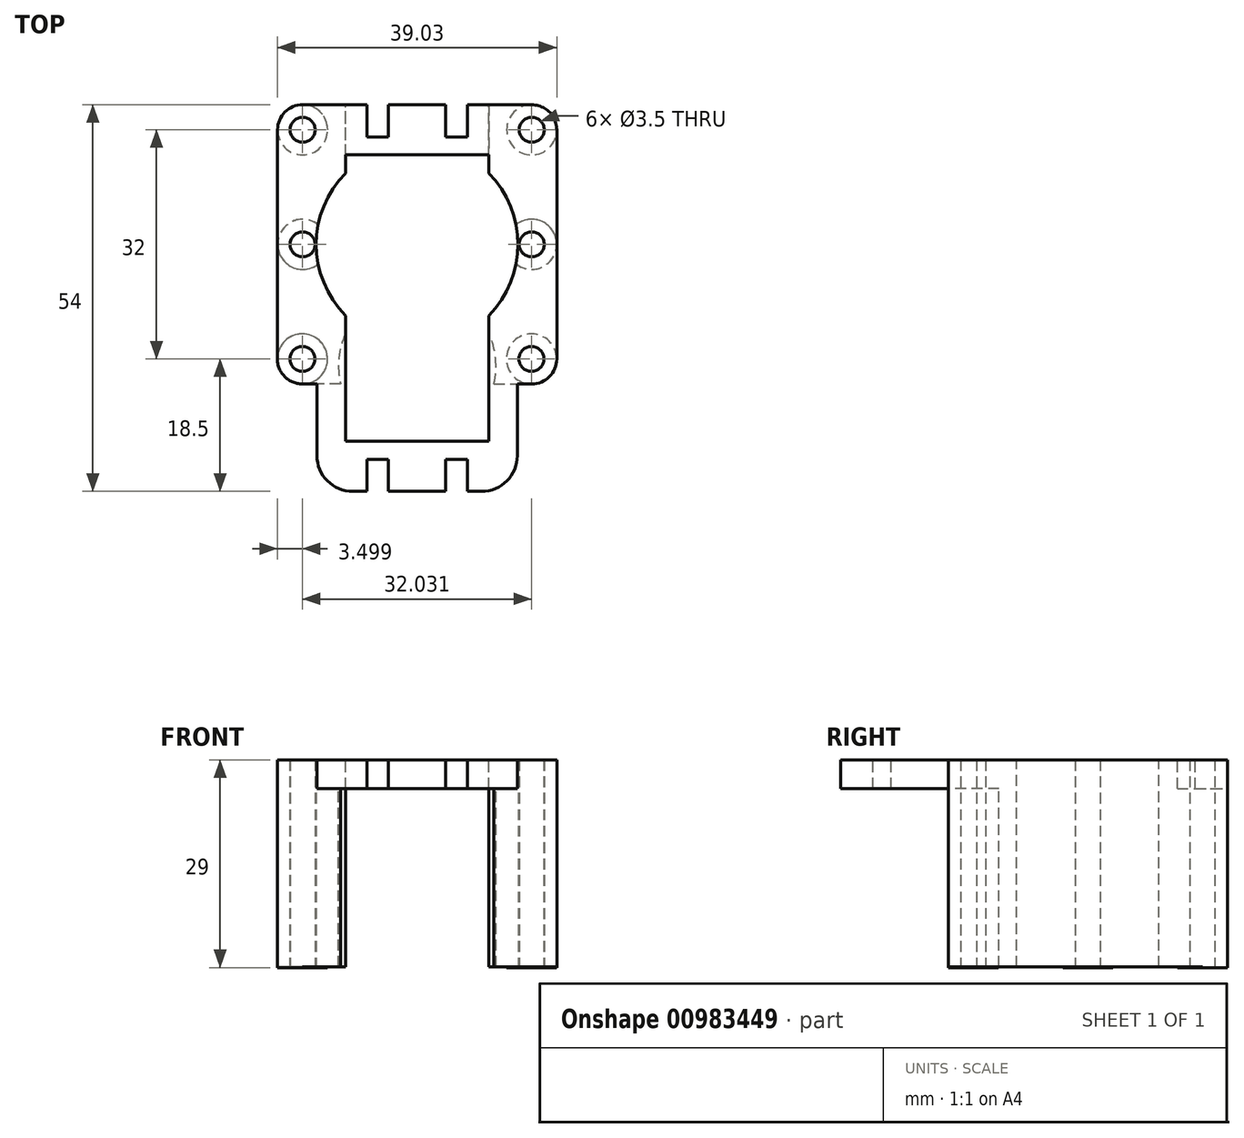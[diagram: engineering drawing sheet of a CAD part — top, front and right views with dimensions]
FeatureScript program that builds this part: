
annotation { "Feature Type Name" : "Feature", "Feature Type Description" : "" }
export const myFeature = defineFeature(function(context is Context, id is Id, definition is map)
    precondition{}
    {
        {
            var Q0;
            Q0=qCreatedBy(makeId("Top.planeOp"),FACE);
            var sketch = newSketch(context, id + "F0", { "sketchPlane" : qUnion([Q0])});
            skCircle(sketch, "E0", {"center": v(-16, 16) * mm, "radius": 3.5 * mm});
            skCircle(sketch, "E1", {"center": v(16, 16) * mm, "radius": 3.5 * mm});
            skCircle(sketch, "E2", {"center": v(15.97, -16) * mm, "radius": 3.5 * mm});
            skCircle(sketch, "E3", {"center": v(-16.03, -16) * mm, "radius": 3.5 * mm});
            skCircle(sketch, "E4", {"center": v(-16, 16) * mm, "radius": 1.75 * mm});
            skCircle(sketch, "E5", {"center": v(16, 16) * mm, "radius": 1.75 * mm});
            skCircle(sketch, "E6", {"center": v(-16.03, -16) * mm, "radius": 1.75 * mm});
            skCircle(sketch, "E7", {"center": v(15.97, -16) * mm, "radius": 1.75 * mm});
            skCircle(sketch, "E8", {"center": v(16, 0) * mm, "radius": 3.5 * mm});
            skCircle(sketch, "E9", {"center": v(16, 0) * mm, "radius": 1.75 * mm});
            skCircle(sketch, "E10", {"center": v(-16, 0) * mm, "radius": 1.75 * mm});
            skCircle(sketch, "E11", {"center": v(-16, 0) * mm, "radius": 3.5 * mm});
            skCircle(sketch, "E12", {"center": v(0, 0) * mm, "radius": 14.1 * mm});
            skSolve(sketch);
        }
        {
            var Q0;
            Q0=makeQuery(id+"F0.imprint","IMPRINT",FACE,{"disambiguationData":[TD([[makeQuery(id+"F0.imprint","IMPRINT",EDGE,{"derivedFrom":sQuery(id+"F0.wireOp",EDGE,"E0")}),1.0]])]});
            var Q1;
            Q1=makeQuery(id+"F0.imprint","IMPRINT",FACE,{"disambiguationData":[TD([[makeQuery(id+"F0.imprint","IMPRINT",EDGE,{"derivedFrom":sQuery(id+"F0.wireOp",EDGE,"E1")}),1.0]])]});
            var Q2;
            Q2=makeQuery(id+"F0.imprint","IMPRINT",FACE,{"disambiguationData":[TD([[makeQuery(id+"F0.imprint","IMPRINT",EDGE,{"derivedFrom":sQuery(id+"F0.wireOp",EDGE,"E2")}),1.0]])]});
            var Q3;
            Q3=makeQuery(id+"F0.imprint","IMPRINT",FACE,{"disambiguationData":[TD([[makeQuery(id+"F0.imprint","IMPRINT",EDGE,{"derivedFrom":sQuery(id+"F0.wireOp",EDGE,"E3")}),1.0]])]});
            var Q4;
            {var subQ0=sQuery(id+"F0.wireOp",EDGE,"aDhAWXYM-tOJJ-d5Va-h822-jFobYjWTLzZv");var subQ1=sQuery(id+"F0.wireOp",EDGE,"E8");var subQ2=makeQuery(id+"F0.imprint","INTERSECT",VERTEX,{"disambiguationData":[OD(0.0)],"derivedFrom":[subQ1,subQ0]});Q4=makeQuery(id+"F0.imprint","IMPRINT",FACE,{"disambiguationData":[TD([[makeQuery(id+"F0.imprint","IMPRINT",EDGE,{"disambiguationData":[TD([[subQ2,1.0]])],"derivedFrom":subQ1}),1.0]])]});}
            var Q5;
            {var subQ0=sQuery(id+"F0.wireOp",EDGE,"aDhAWXYM-tOJJ-d5Va-h822-jFobYjWTLzZv");var subQ1=sQuery(id+"F0.wireOp",EDGE,"E10");var subQ2=makeQuery(id+"F0.imprint","INTERSECT",VERTEX,{"disambiguationData":[OD(0.0)],"derivedFrom":[subQ1,subQ0]});Q5=makeQuery(id+"F0.imprint","IMPRINT",FACE,{"disambiguationData":[TD([[makeQuery(id+"F0.imprint","IMPRINT",EDGE,{"disambiguationData":[TD([[subQ2,-1.0]])],"derivedFrom":subQ1}),-1.0]])]});}
            extrude(context, id + "F1", {"entities" : qUnion([Q0, Q1, Q2, Q3, Q4, Q5]), "depth" : 29 * mm, "offsetDistance" : 25 * mm});
        }
        {
            var Q0;
            Q0=makeQuery(id+"F1.opExtrude","CAP_FACE",FACE,{"disambiguationData":[OSD([sQuery(id+"F0.wireOp",EDGE,"E0"),sQuery(id+"F0.wireOp",EDGE,"E4")])],"isStart":false});
            var sketch = newSketch(context, id + "F2", { "sketchPlane" : qUnion([Q0])});
            skLineSegment(sketch, "E13.bottom", {"start": v(10, -19.5) * mm, "end": v(-10, -19.5) * mm});
            skLineSegment(sketch, "E13.top", {"start": v(10, 19.5) * mm, "end": v(-10, 19.5) * mm});
            skLineSegment(sketch, "E13.left", {"start": v(10, -19.5) * mm, "end": v(10, 19.5) * mm});
            skLineSegment(sketch, "E13.right", {"start": v(-10, -19.5) * mm, "end": v(-10, 19.5) * mm});
            skPoint(sketch, "E13.middle", {"position": v(0, 0) * mm});
            skLineSegment(sketch, "E14.bottom", {"start": v(-10, 19.5) * mm, "end": v(-16, 19.5) * mm});
            skLineSegment(sketch, "E14.top", {"start": v(-10, -19.5) * mm, "end": v(-16, -19.5) * mm});
            skLineSegment(sketch, "E14.left", {"start": v(-10, 19.5) * mm, "end": v(-10, -19.5) * mm});
            skLineSegment(sketch, "E14.right", {"start": v(-19.5, 16) * mm, "end": v(-19.5, -16) * mm});
            skLineSegment(sketch, "E15.bottom", {"start": v(10, 19.5) * mm, "end": v(16, 19.5) * mm});
            skLineSegment(sketch, "E15.top", {"start": v(10, -19.5) * mm, "end": v(16, -19.5) * mm});
            skLineSegment(sketch, "E15.left", {"start": v(10, 19.5) * mm, "end": v(10, -19.5) * mm});
            skLineSegment(sketch, "E15.right", {"start": v(19.5, 16) * mm, "end": v(19.5, -16) * mm});
            skPoint(sketch, "E16.visualSharp", {"position": v(-19.5, 19.5) * mm});
            skArc(sketch, "E16.filletArc", {"start": v(-16, 19.5) * mm, "mid": v(-18.47, 18.47) * mm, "end": v(-19.5, 16) * mm});
            skPoint(sketch, "E17.visualSharp", {"position": v(19.5, 19.5) * mm});
            skArc(sketch, "E17.filletArc", {"start": v(19.5, 16) * mm, "mid": v(18.47, 18.47) * mm, "end": v(16, 19.5) * mm});
            skPoint(sketch, "E18.visualSharp", {"position": v(19.5, -19.5) * mm});
            skArc(sketch, "E18.filletArc", {"start": v(16, -19.5) * mm, "mid": v(18.47, -18.47) * mm, "end": v(19.5, -16) * mm});
            skPoint(sketch, "E19.visualSharp", {"position": v(-19.5, -19.5) * mm});
            skArc(sketch, "E19.filletArc", {"start": v(-19.5, -16) * mm, "mid": v(-18.47, -18.47) * mm, "end": v(-16, -19.5) * mm});
            skCircle(sketch, "E20", {"center": v(0, 0) * mm, "radius": 14.1 * mm});
            skCircle(sketch, "E21", {"center": v(0, -17) * mm, "radius": 11 * mm});
            skSolve(sketch);
        }
        {
            var Q0;
            Q0=makeQuery(id+"F2.imprint","IMPRINT",FACE,{"disambiguationData":[TD([[makeQuery(id+"F2.imprint","IMPRINT",EDGE,{"derivedFrom":sQuery(id+"F2.wireOp",EDGE,"E15.bottom")}),-1.0]])]});
            var Q1;
            {var subQ2=sQuery(id+"F2.wireOp",EDGE,"E14.bottom");Q1=makeQuery(id+"F2.imprint","IMPRINT",FACE,{"disambiguationData":[TD([[makeQuery(id+"F2.imprint","IMPRINT",EDGE,{"derivedFrom":subQ2}),1.0]])]});}
            extrude(context, id + "F3", {"entities" : qUnion([Q0, Q1]), "operationType" : NewBodyOperationType.ADD, "oppositeDirection" : true, "depth" : 28.9 * mm, "offsetDistance" : 25 * mm});
        }
        {
            var Q0;
            Q0=makeQuery(id+"F3.boolean.opBoolean","MERGE",FACE,{"derivedFrom":[makeQuery(id+"F1.opExtrude","CAP_FACE",FACE,{"disambiguationData":[OSD([sQuery(id+"F0.wireOp",EDGE,"E0"),sQuery(id+"F0.wireOp",EDGE,"E4")])],"isStart":false}),makeQuery(id+"F1.opExtrude","CAP_FACE",FACE,{"disambiguationData":[OSD([sQuery(id+"F0.wireOp",EDGE,"E3"),sQuery(id+"F0.wireOp",EDGE,"E6")])],"isStart":false}),makeQuery(id+"F3.opExtrude","CAP_FACE",FACE,{"disambiguationData":[OSD([sQuery(id+"F2.wireOp",EDGE,"E14.bottom"),sQuery(id+"F2.wireOp",EDGE,"E14.top"),sQuery(id+"F2.wireOp",EDGE,"E14.left"),sQuery(id+"F2.wireOp",EDGE,"E14.right"),sQuery(id+"F2.wireOp",EDGE,"E16.filletArc"),sQuery(id+"F2.wireOp",EDGE,"E19.filletArc")])],"isStart":true})]});
            var sketch = newSketch(context, id + "F4", { "sketchPlane" : qUnion([Q0])});
            skLineSegment(sketch, "E22.bottom", {"start": v(-10, 19.5) * mm, "end": v(10, 19.5) * mm});
            skLineSegment(sketch, "E22.top", {"start": v(-10, 12.5) * mm, "end": v(10, 12.5) * mm});
            skLineSegment(sketch, "E22.left", {"start": v(-10, 19.5) * mm, "end": v(-10, 12.5) * mm});
            skLineSegment(sketch, "E22.right", {"start": v(10, 19.5) * mm, "end": v(10, 12.5) * mm});
            skLineSegment(sketch, "E23.bottom", {"start": v(-4, 15) * mm, "end": v(-7, 15) * mm});
            skLineSegment(sketch, "E23.top", {"start": v(-4, 19.5) * mm, "end": v(-7, 19.5) * mm});
            skLineSegment(sketch, "E23.left", {"start": v(-4, 15) * mm, "end": v(-4, 19.5) * mm});
            skLineSegment(sketch, "E23.right", {"start": v(-7, 15) * mm, "end": v(-7, 19.5) * mm});
            skPoint(sketch, "E23.middle", {"position": v(-5.5, 17.25) * mm});
            skLineSegment(sketch, "E24.bottom", {"start": v(7, 15) * mm, "end": v(4, 15) * mm});
            skLineSegment(sketch, "E24.top", {"start": v(7, 19.5) * mm, "end": v(4, 19.5) * mm});
            skLineSegment(sketch, "E24.left", {"start": v(7, 15) * mm, "end": v(7, 19.5) * mm});
            skLineSegment(sketch, "E24.right", {"start": v(4, 15) * mm, "end": v(4, 19.5) * mm});
            skPoint(sketch, "E24.middle", {"position": v(5.5, 17.25) * mm});
            skSolve(sketch);
        }
        {
            var Q0;
            Q0=makeQuery(id+"F4.imprint","IMPRINT",FACE,{"disambiguationData":[TD([[makeQuery(id+"F4.imprint","IMPRINT",EDGE,{"derivedFrom":sQuery(id+"F4.wireOp",EDGE,"E22.top")}),1.0]])]});
            extrude(context, id + "F5", {"entities" : qUnion([Q0]), "operationType" : NewBodyOperationType.ADD, "oppositeDirection" : true, "depth" : 4 * mm, "offsetDistance" : 25 * mm});
        }
        {
            var Q0;
            {var subQ0=sQuery(id+"F2.wireOp",EDGE,"E21");var subQ1=sQuery(id+"F2.wireOp",EDGE,"E20");var subQ2=sQuery(id+"F0.wireOp",EDGE,"E12");var subQ3=sQuery(id+"F0.wireOp",EDGE,"E0");Q0=makeQuery(id+"F5.boolean.opBoolean","MERGE",FACE,{"derivedFrom":[makeQuery(id+"F3.boolean.opBoolean","MERGE",FACE,{"derivedFrom":[makeQuery(id+"F1.opExtrude","CAP_FACE",FACE,{"disambiguationData":[OSD([subQ3,sQuery(id+"F0.wireOp",EDGE,"E4")])],"isStart":false}),makeQuery(id+"F1.opExtrude","CAP_FACE",FACE,{"disambiguationData":[OSD([sQuery(id+"F0.wireOp",EDGE,"E3"),sQuery(id+"F0.wireOp",EDGE,"E6")])],"isStart":false}),makeQuery(id+"F1.opExtrude","CAP_FACE",FACE,{"disambiguationData":[OSD([sQuery(id+"F0.wireOp",EDGE,"E10"),sQuery(id+"F0.wireOp",EDGE,"E11"),subQ2])],"isStart":false}),makeQuery(id+"F3.opExtrude","CAP_FACE",FACE,{"disambiguationData":[OSD([subQ3,sQuery(id+"F2.wireOp",EDGE,"E14.bottom"),sQuery(id+"F2.wireOp",EDGE,"E14.top"),sQuery(id+"F2.wireOp",EDGE,"E14.left"),sQuery(id+"F2.wireOp",EDGE,"E14.right"),sQuery(id+"F2.wireOp",EDGE,"E19.filletArc"),subQ1,subQ0])],"isStart":true})]}),makeQuery(id+"F3.boolean.opBoolean","MERGE",FACE,{"derivedFrom":[makeQuery(id+"F1.opExtrude","CAP_FACE",FACE,{"disambiguationData":[OSD([sQuery(id+"F0.wireOp",EDGE,"E1"),sQuery(id+"F0.wireOp",EDGE,"E5")])],"isStart":false}),makeQuery(id+"F1.opExtrude","CAP_FACE",FACE,{"disambiguationData":[OSD([sQuery(id+"F0.wireOp",EDGE,"E2"),sQuery(id+"F0.wireOp",EDGE,"E7")])],"isStart":false}),makeQuery(id+"F1.opExtrude","CAP_FACE",FACE,{"disambiguationData":[OSD([sQuery(id+"F0.wireOp",EDGE,"E8"),sQuery(id+"F0.wireOp",EDGE,"E9"),subQ2])],"isStart":false}),makeQuery(id+"F3.opExtrude","CAP_FACE",FACE,{"disambiguationData":[OSD([sQuery(id+"F2.wireOp",EDGE,"E15.bottom"),sQuery(id+"F2.wireOp",EDGE,"E15.top"),sQuery(id+"F2.wireOp",EDGE,"E15.left"),sQuery(id+"F2.wireOp",EDGE,"E15.right"),sQuery(id+"F2.wireOp",EDGE,"E17.filletArc"),sQuery(id+"F2.wireOp",EDGE,"E18.filletArc"),subQ1,subQ0])],"isStart":true})]}),makeQuery(id+"F5.opExtrude","CAP_FACE",FACE,{"disambiguationData":[OSD([sQuery(id+"F4.wireOp",EDGE,"E22.bottom"),sQuery(id+"F4.wireOp",EDGE,"E22.top"),sQuery(id+"F4.wireOp",EDGE,"E22.left"),sQuery(id+"F4.wireOp",EDGE,"E22.right"),sQuery(id+"F4.wireOp",EDGE,"E23.bottom"),sQuery(id+"F4.wireOp",EDGE,"E23.left"),sQuery(id+"F4.wireOp",EDGE,"E23.right"),sQuery(id+"F4.wireOp",EDGE,"E24.bottom"),sQuery(id+"F4.wireOp",EDGE,"E24.left"),sQuery(id+"F4.wireOp",EDGE,"E24.right")])],"isStart":true})]});}
            var sketch = newSketch(context, id + "F6", { "sketchPlane" : qUnion([Q0])});
            skLineSegment(sketch, "E25.bottom", {"start": v(-10, 12.5) * mm, "end": v(10, 12.5) * mm});
            skLineSegment(sketch, "E25.top", {"start": v(-10, -27.5) * mm, "end": v(10, -27.5) * mm});
            skLineSegment(sketch, "E25.left", {"start": v(-10, 12.5) * mm, "end": v(-10, -27.5) * mm});
            skLineSegment(sketch, "E25.right", {"start": v(10, 12.5) * mm, "end": v(10, -27.5) * mm});
            skLineSegment(sketch, "E26.bottom", {"start": v(9, -34.5) * mm, "end": v(-9, -34.5) * mm});
            skLineSegment(sketch, "E26.top", {"start": v(14, -19.5) * mm, "end": v(-14, -19.5) * mm});
            skLineSegment(sketch, "E26.left", {"start": v(14, -29.5) * mm, "end": v(14, -19.5) * mm});
            skLineSegment(sketch, "E26.right", {"start": v(-14, -29.5) * mm, "end": v(-14, -19.5) * mm});
            skPoint(sketch, "E26.middle", {"position": v(0, -27) * mm});
            skLineSegment(sketch, "E27.bottom", {"start": v(-4, -34.5) * mm, "end": v(-7, -34.5) * mm});
            skLineSegment(sketch, "E27.top", {"start": v(-4, -30) * mm, "end": v(-7, -30) * mm});
            skLineSegment(sketch, "E27.left", {"start": v(-4, -34.5) * mm, "end": v(-4, -30) * mm});
            skLineSegment(sketch, "E27.right", {"start": v(-7, -34.5) * mm, "end": v(-7, -30) * mm});
            skPoint(sketch, "E27.middle", {"position": v(-5.5, -32.25) * mm});
            skLineSegment(sketch, "E28.bottom", {"start": v(7, -34.5) * mm, "end": v(4, -34.5) * mm});
            skLineSegment(sketch, "E28.top", {"start": v(7, -30) * mm, "end": v(4, -30) * mm});
            skLineSegment(sketch, "E28.left", {"start": v(7, -34.5) * mm, "end": v(7, -30) * mm});
            skLineSegment(sketch, "E28.right", {"start": v(4, -34.5) * mm, "end": v(4, -30) * mm});
            skPoint(sketch, "E28.middle", {"position": v(5.5, -32.25) * mm});
            skPoint(sketch, "E29.visualSharp", {"position": v(-14, -34.5) * mm});
            skArc(sketch, "E29.filletArc", {"start": v(-14, -29.5) * mm, "mid": v(-12.54, -33.04) * mm, "end": v(-9, -34.5) * mm});
            skPoint(sketch, "E30.visualSharp", {"position": v(14, -34.5) * mm});
            skArc(sketch, "E30.filletArc", {"start": v(9, -34.5) * mm, "mid": v(12.54, -33.04) * mm, "end": v(14, -29.5) * mm});
            skLineSegment(sketch, "E31.bottom", {"start": v(14, -19.5) * mm, "end": v(10, -19.5) * mm});
            skLineSegment(sketch, "E31.top", {"start": v(14, -9.94) * mm, "end": v(10, -9.94) * mm});
            skLineSegment(sketch, "E31.left", {"start": v(14, -19.5) * mm, "end": v(14, -9.94) * mm});
            skLineSegment(sketch, "E31.right", {"start": v(10, -19.5) * mm, "end": v(10, -9.94) * mm});
            skLineSegment(sketch, "E32.bottom", {"start": v(-14, -19.5) * mm, "end": v(-10, -19.5) * mm});
            skLineSegment(sketch, "E32.top", {"start": v(-14, -9.94) * mm, "end": v(-10, -9.94) * mm});
            skLineSegment(sketch, "E32.left", {"start": v(-14, -19.5) * mm, "end": v(-14, -9.94) * mm});
            skLineSegment(sketch, "E32.right", {"start": v(-10, -19.5) * mm, "end": v(-10, -9.94) * mm});
            skSolve(sketch);
        }
        {
            var Q0;
            {var subQ16=sQuery(id+"F6.wireOp",EDGE,"E25.top");Q0=makeQuery(id+"F6.imprint","IMPRINT",FACE,{"disambiguationData":[TD([[makeQuery(id+"F6.imprint","IMPRINT",EDGE,{"derivedFrom":subQ16}),-1.0]])]});}
            var Q1;
            {var subQ1=sQuery(id+"F2.wireOp",EDGE,"E21");var subQ2=makeQuery(id+"F3.opExtrude","CAP_EDGE",EDGE,{"disambiguationData":[OSD([subQ1]),TDD([makeQuery(id+"F2.imprint","IMPRINT",EDGE,{"disambiguationData":[TD([[makeQuery(id+"F2.imprint","INTERSECT",VERTEX,{"derivedFrom":[sQuery(id+"F2.wireOp",EDGE,"E15.top"),subQ1]}),-1.0]])],"derivedFrom":subQ1})])],"isStart":true});Q1=makeQuery(id+"F6.imprint","IMPRINT",FACE,{"disambiguationData":[TD([[makeQuery(id+"F6.imprint","IMPRINT",EDGE,{"derivedFrom":subQ2}),1.0]])]});}
            var Q2;
            {var subQ1=sQuery(id+"F2.wireOp",EDGE,"E21");var subQ2=makeQuery(id+"F3.opExtrude","CAP_EDGE",EDGE,{"disambiguationData":[OSD([subQ1]),TDD([makeQuery(id+"F2.imprint","IMPRINT",EDGE,{"disambiguationData":[TD([[makeQuery(id+"F2.imprint","INTERSECT",VERTEX,{"derivedFrom":[sQuery(id+"F2.wireOp",EDGE,"E14.top"),subQ1]}),1.0]])],"derivedFrom":subQ1})])],"isStart":true});Q2=makeQuery(id+"F6.imprint","IMPRINT",FACE,{"disambiguationData":[TD([[makeQuery(id+"F6.imprint","IMPRINT",EDGE,{"derivedFrom":subQ2}),1.0]])]});}
            extrude(context, id + "F7", {"entities" : qUnion([Q0, Q1, Q2]), "operationType" : NewBodyOperationType.ADD, "oppositeDirection" : true, "depth" : 4 * mm, "offsetDistance" : 25 * mm});
        }
        {
            var Q0;
            Q0=makeQuery(id+"F3.boolean.opBoolean","SPLIT",FACE,{"disambiguationData":[TD([makeQuery(id+"F1.opExtrude","SWEPT_FACE",FACE,{"disambiguationData":[OSD([sQuery(id+"F0.wireOp",EDGE,"E7")])]})])],"derivedFrom":makeQuery(id+"F3.opExtrude","CAP_FACE",FACE,{"disambiguationData":[OSD([sQuery(id+"F2.wireOp",EDGE,"E15.bottom"),sQuery(id+"F2.wireOp",EDGE,"E15.top"),sQuery(id+"F2.wireOp",EDGE,"E15.left"),sQuery(id+"F2.wireOp",EDGE,"E15.right"),sQuery(id+"F2.wireOp",EDGE,"E17.filletArc"),sQuery(id+"F2.wireOp",EDGE,"E18.filletArc")])],"isStart":false})});
            var sketch = newSketch(context, id + "F8", { "sketchPlane" : qUnion([Q0])});
            skSolve(sketch);
        }
        {
            var Q0;
            Q0 = qSketchRegion(id + "F8", true);
            var Q1;
            Q1=makeQuery(id+"F3.boolean.opBoolean","SPLIT",FACE,{"disambiguationData":[TD([makeQuery(id+"F1.opExtrude","SWEPT_FACE",FACE,{"disambiguationData":[OSD([sQuery(id+"F0.wireOp",EDGE,"E6")])]})])],"derivedFrom":makeQuery(id+"F3.opExtrude","CAP_FACE",FACE,{"disambiguationData":[OSD([sQuery(id+"F2.wireOp",EDGE,"E14.bottom"),sQuery(id+"F2.wireOp",EDGE,"E14.top"),sQuery(id+"F2.wireOp",EDGE,"E14.left"),sQuery(id+"F2.wireOp",EDGE,"E14.right"),sQuery(id+"F2.wireOp",EDGE,"E16.filletArc"),sQuery(id+"F2.wireOp",EDGE,"E19.filletArc")])],"isStart":false})});
            var Q2;
            Q2=makeQuery(id+"F3.boolean.opBoolean","SPLIT",FACE,{"disambiguationData":[TD([makeQuery(id+"F1.opExtrude","SWEPT_FACE",FACE,{"disambiguationData":[OSD([sQuery(id+"F0.wireOp",EDGE,"E10")])]})])],"derivedFrom":makeQuery(id+"F3.opExtrude","CAP_FACE",FACE,{"disambiguationData":[OSD([sQuery(id+"F2.wireOp",EDGE,"E14.bottom"),sQuery(id+"F2.wireOp",EDGE,"E14.top"),sQuery(id+"F2.wireOp",EDGE,"E14.left"),sQuery(id+"F2.wireOp",EDGE,"E14.right"),sQuery(id+"F2.wireOp",EDGE,"E16.filletArc"),sQuery(id+"F2.wireOp",EDGE,"E19.filletArc")])],"isStart":false})});
            var Q3;
            Q3=makeQuery(id+"F3.boolean.opBoolean","SPLIT",FACE,{"disambiguationData":[TD([makeQuery(id+"F1.opExtrude","SWEPT_FACE",FACE,{"disambiguationData":[OSD([sQuery(id+"F0.wireOp",EDGE,"E9")])]})])],"derivedFrom":makeQuery(id+"F3.opExtrude","CAP_FACE",FACE,{"disambiguationData":[OSD([sQuery(id+"F2.wireOp",EDGE,"E15.bottom"),sQuery(id+"F2.wireOp",EDGE,"E15.top"),sQuery(id+"F2.wireOp",EDGE,"E15.left"),sQuery(id+"F2.wireOp",EDGE,"E15.right"),sQuery(id+"F2.wireOp",EDGE,"E17.filletArc"),sQuery(id+"F2.wireOp",EDGE,"E18.filletArc")])],"isStart":false})});
            var Q4;
            Q4=makeQuery(id+"F3.boolean.opBoolean","SPLIT",FACE,{"disambiguationData":[TD([makeQuery(id+"F1.opExtrude","SWEPT_FACE",FACE,{"disambiguationData":[OSD([sQuery(id+"F0.wireOp",EDGE,"E5")])]})])],"derivedFrom":makeQuery(id+"F3.opExtrude","CAP_FACE",FACE,{"disambiguationData":[OSD([sQuery(id+"F2.wireOp",EDGE,"E15.bottom"),sQuery(id+"F2.wireOp",EDGE,"E15.top"),sQuery(id+"F2.wireOp",EDGE,"E15.left"),sQuery(id+"F2.wireOp",EDGE,"E15.right"),sQuery(id+"F2.wireOp",EDGE,"E17.filletArc"),sQuery(id+"F2.wireOp",EDGE,"E18.filletArc")])],"isStart":false})});
            var Q5;
            Q5=makeQuery(id+"F3.boolean.opBoolean","SPLIT",FACE,{"disambiguationData":[TD([makeQuery(id+"F1.opExtrude","SWEPT_FACE",FACE,{"disambiguationData":[OSD([sQuery(id+"F0.wireOp",EDGE,"E4")])]})])],"derivedFrom":makeQuery(id+"F3.opExtrude","CAP_FACE",FACE,{"disambiguationData":[OSD([sQuery(id+"F2.wireOp",EDGE,"E14.bottom"),sQuery(id+"F2.wireOp",EDGE,"E14.top"),sQuery(id+"F2.wireOp",EDGE,"E14.left"),sQuery(id+"F2.wireOp",EDGE,"E14.right"),sQuery(id+"F2.wireOp",EDGE,"E16.filletArc"),sQuery(id+"F2.wireOp",EDGE,"E19.filletArc")])],"isStart":false})});
            var Q6;
            Q6=makeQuery(id+"F8.imprint","IMPRINT",FACE,{"disambiguationData":[TD([[makeQuery(id+"F8.imprint","IMPRINT",EDGE,{"derivedFrom":makeQuery(id+"F3.boolean.opBoolean","INTERSECT",EDGE,{"derivedFrom":[makeQuery(id+"F1.opExtrude","SWEPT_FACE",FACE,{"disambiguationData":[OSD([sQuery(id+"F0.wireOp",EDGE,"E7")])]}),makeQuery(id+"F3.opExtrude","CAP_FACE",FACE,{"disambiguationData":[OSD([sQuery(id+"F2.wireOp",EDGE,"E15.bottom"),sQuery(id+"F2.wireOp",EDGE,"E15.top"),sQuery(id+"F2.wireOp",EDGE,"E15.left"),sQuery(id+"F2.wireOp",EDGE,"E15.right"),sQuery(id+"F2.wireOp",EDGE,"E17.filletArc"),sQuery(id+"F2.wireOp",EDGE,"E18.filletArc")])],"isStart":false})]})}),-1.0]])]});
            extrude(context, id + "F9", {"entities" : qUnion([Q0, Q1, Q2, Q3, Q4, Q5, Q6]), "operationType" : NewBodyOperationType.REMOVE, "oppositeDirection" : true, "depth" : 35 * mm, "offsetDistance" : 25 * mm});
        }
    });
